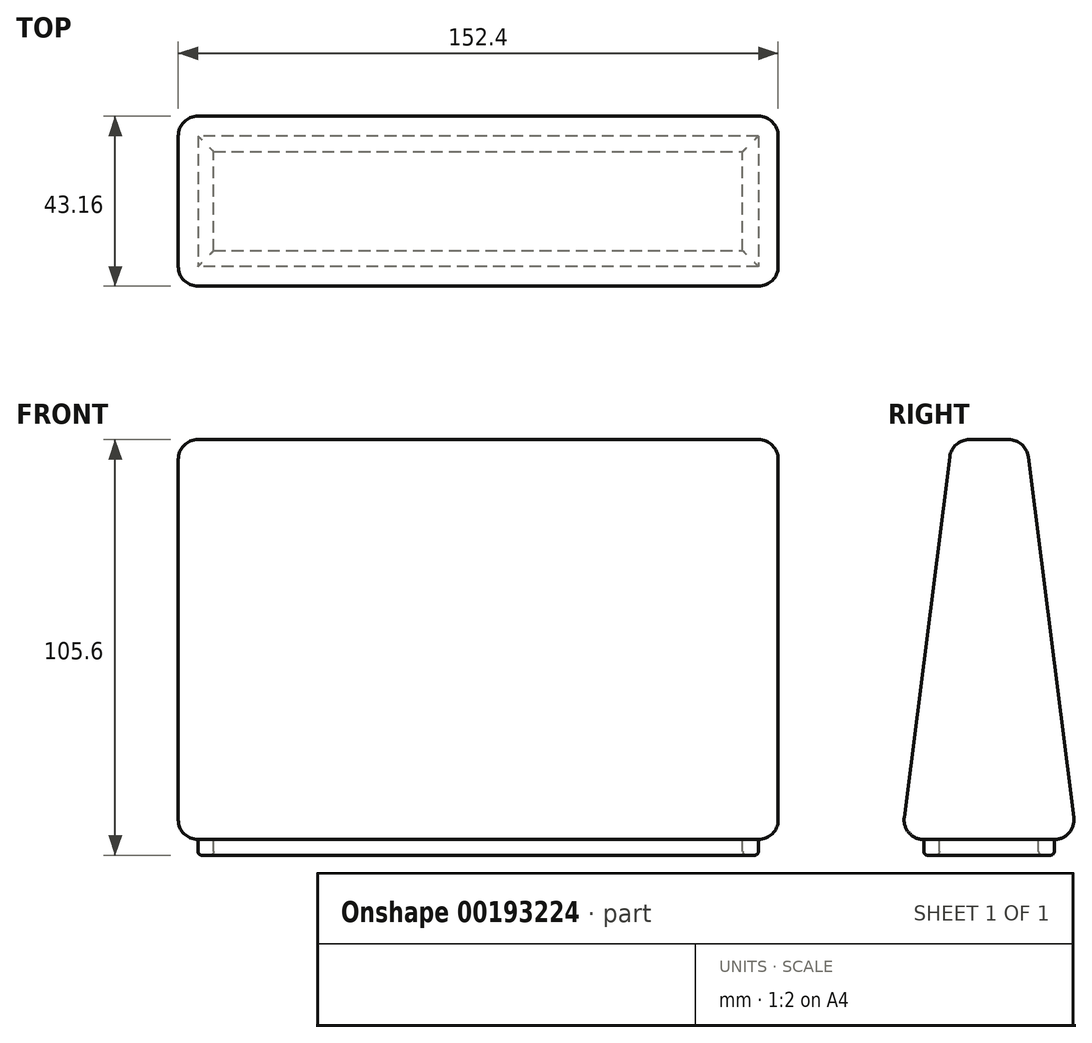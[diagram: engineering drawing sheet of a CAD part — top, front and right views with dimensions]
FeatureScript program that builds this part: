
annotation { "Feature Type Name" : "Feature", "Feature Type Description" : "" }
export const myFeature = defineFeature(function(context is Context, id is Id, definition is map)
    precondition{}
    {
        {
            var Q0;
            Q0=qCreatedBy(makeId("Right.planeOp"),FACE);
            var sketch = newSketch(context, id + "F0", { "sketchPlane" : qUnion([Q0])});
            skLineSegment(sketch, "E0", {"start": v(0, -83.95) * mm, "end": v(0, 33) * mm, "construction": true});
            skLineSegment(sketch, "E1", {"start": v(0, -83.95) * mm, "end": v(22.26, -83.95) * mm});
            skLineSegment(sketch, "E2", {"start": v(22.26, -83.95) * mm, "end": v(9.4, 17.65) * mm});
            skLineSegment(sketch, "E3", {"start": v(9.4, 17.65) * mm, "end": v(0, 17.65) * mm});
            skLineSegment(sketch, "E4.MirrorCS", {"start": v(0, -83.95) * mm, "end": v(-22.26, -83.95) * mm});
            skLineSegment(sketch, "E5.MirrorCS", {"start": v(-22.26, -83.95) * mm, "end": v(-9.4, 17.65) * mm});
            skLineSegment(sketch, "E6.MirrorCS", {"start": v(-9.4, 17.65) * mm, "end": v(0, 17.65) * mm});
            skSolve(sketch);
        }
        {
            var Q0;
            Q0=makeQuery(id+"F0.imprint","IMPRINT",FACE,{"disambiguationData":[TD([[makeQuery(id+"F0.imprint","IMPRINT",EDGE,{"derivedFrom":sQuery(id+"F0.wireOp",EDGE,"E1")}),1.0]])]});
            extrude(context, id + "F1", {"entities" : qUnion([Q0]), "depth" : 152.4 * mm});
        }
        {
            var Q0;
            Q0=makeQuery(id+"F1.opExtrude","SWEPT_FACE",FACE,{"disambiguationData":[OSD([sQuery(id+"F0.wireOp",EDGE,"E2")])]});
            var Q1;
            Q1=makeQuery(id+"F1.opExtrude","SWEPT_FACE",FACE,{"disambiguationData":[OSD([sQuery(id+"F0.wireOp",EDGE,"E5.MirrorCS")])]});
            var Q2;
            Q2=makeQuery(id+"F1.opExtrude","SWEPT_FACE",FACE,{"disambiguationData":[OSD([sQuery(id+"F0.wireOp",EDGE,"E3"),sQuery(id+"F0.wireOp",EDGE,"E6.MirrorCS")])]});
            var Q3;
            Q3=makeQuery(id+"F1.opExtrude","SWEPT_EDGE",EDGE,{"disambiguationData":[OSD([sQuery(id+"F0.wireOp",EDGE,"E5.MirrorCS"),sQuery(id+"F0.wireOp",EDGE,"E6.MirrorCS")])]});
            var Q4;
            Q4=makeQuery(id+"F1.opExtrude","SWEPT_EDGE",EDGE,{"disambiguationData":[OSD([sQuery(id+"F0.wireOp",EDGE,"E4.MirrorCS"),sQuery(id+"F0.wireOp",EDGE,"E5.MirrorCS")])]});
            var Q5;
            Q5=makeQuery(id+"F1.opExtrude","CAP_FACE",FACE,{"disambiguationData":[OSD([sQuery(id+"F0.wireOp",EDGE,"E1"),sQuery(id+"F0.wireOp",EDGE,"E2"),sQuery(id+"F0.wireOp",EDGE,"E3"),sQuery(id+"F0.wireOp",EDGE,"E4.MirrorCS"),sQuery(id+"F0.wireOp",EDGE,"E5.MirrorCS"),sQuery(id+"F0.wireOp",EDGE,"E6.MirrorCS")])],"isStart":false});
            var Q6;
            Q6=makeQuery(id+"F1.opExtrude","SWEPT_EDGE",EDGE,{"disambiguationData":[OSD([sQuery(id+"F0.wireOp",EDGE,"E2"),sQuery(id+"F0.wireOp",EDGE,"E3")])]});
            var Q7;
            Q7=makeQuery(id+"F1.opExtrude","CAP_FACE",FACE,{"disambiguationData":[OSD([sQuery(id+"F0.wireOp",EDGE,"E1"),sQuery(id+"F0.wireOp",EDGE,"E2"),sQuery(id+"F0.wireOp",EDGE,"E3"),sQuery(id+"F0.wireOp",EDGE,"E4.MirrorCS"),sQuery(id+"F0.wireOp",EDGE,"E5.MirrorCS"),sQuery(id+"F0.wireOp",EDGE,"E6.MirrorCS")])],"isStart":true});
            var Q8;
            Q8=makeQuery(id+"F1.opExtrude","CAP_EDGE",EDGE,{"disambiguationData":[OSD([sQuery(id+"F0.wireOp",EDGE,"E5.MirrorCS")])],"isStart":true});
            var Q9;
            Q9=makeQuery(id+"F1.opExtrude","CAP_EDGE",EDGE,{"disambiguationData":[OSD([sQuery(id+"F0.wireOp",EDGE,"E5.MirrorCS")])],"isStart":false});
            var Q10;
            Q10=makeQuery(id+"F1.opExtrude","CAP_EDGE",EDGE,{"disambiguationData":[OSD([sQuery(id+"F0.wireOp",EDGE,"E2")])],"isStart":true});
            var Q11;
            Q11=makeQuery(id+"F1.opExtrude","CAP_EDGE",EDGE,{"disambiguationData":[OSD([sQuery(id+"F0.wireOp",EDGE,"E1"),sQuery(id+"F0.wireOp",EDGE,"E4.MirrorCS")])],"isStart":true});
            var Q12;
            Q12=makeQuery(id+"F1.opExtrude","CAP_EDGE",EDGE,{"disambiguationData":[OSD([sQuery(id+"F0.wireOp",EDGE,"E1"),sQuery(id+"F0.wireOp",EDGE,"E4.MirrorCS")])],"isStart":false});
            var Q13;
            Q13=makeQuery(id+"F1.opExtrude","SWEPT_FACE",FACE,{"disambiguationData":[OSD([sQuery(id+"F0.wireOp",EDGE,"E1"),sQuery(id+"F0.wireOp",EDGE,"E4.MirrorCS")])]});
            var Q14;
            Q14=makeQuery(id+"F1.opExtrude","SWEPT_EDGE",EDGE,{"disambiguationData":[OSD([sQuery(id+"F0.wireOp",EDGE,"E1"),sQuery(id+"F0.wireOp",EDGE,"E2")])]});
            var Q15;
            Q15=makeQuery(id+"F1.opExtrude","CAP_EDGE",EDGE,{"disambiguationData":[OSD([sQuery(id+"F0.wireOp",EDGE,"E2")])],"isStart":false});
            var Q16;
            Q16=makeQuery(id+"F1.opExtrude","CAP_EDGE",EDGE,{"disambiguationData":[OSD([sQuery(id+"F0.wireOp",EDGE,"E3"),sQuery(id+"F0.wireOp",EDGE,"E6.MirrorCS")])],"isStart":true});
            var Q17;
            Q17=makeQuery(id+"F1.opExtrude","CAP_EDGE",EDGE,{"disambiguationData":[OSD([sQuery(id+"F0.wireOp",EDGE,"E3"),sQuery(id+"F0.wireOp",EDGE,"E6.MirrorCS")])],"isStart":false});
            fillet(context, id + "F2", {"entities" : qUnion([Q0, Q1, Q2, Q3, Q4, Q5, Q6, Q7, Q8, Q9, Q10, Q11, Q12, Q13, Q14, Q15, Q16, Q17]), "radius" : 5 * mm, "tangentPropagation" : true, "allowEdgeOverflow" : false});
        }
        {
            var Q0;
            Q0=makeQuery(id+"F1.opExtrude","SWEPT_FACE",FACE,{"disambiguationData":[OSD([sQuery(id+"F0.wireOp",EDGE,"E1"),sQuery(id+"F0.wireOp",EDGE,"E4.MirrorCS")])]});
            var sketch = newSketch(context, id + "F3", { "sketchPlane" : qUnion([Q0])});
            skLineSegment(sketch, "E7.bottom", {"start": v(5, 16.58) * mm, "end": v(147.4, 16.58) * mm});
            skLineSegment(sketch, "E7.top", {"start": v(5, -16.58) * mm, "end": v(147.4, -16.58) * mm});
            skLineSegment(sketch, "E7.left", {"start": v(5, 16.58) * mm, "end": v(5, -16.58) * mm});
            skLineSegment(sketch, "E7.right", {"start": v(147.4, 16.58) * mm, "end": v(147.4, -16.58) * mm});
            skLineSegment(sketch, "E8.0", {"start": v(9, 12.58) * mm, "end": v(9, -12.58) * mm});
            skLineSegment(sketch, "E8.1", {"start": v(9, 12.58) * mm, "end": v(143.4, 12.58) * mm});
            skLineSegment(sketch, "E8.2", {"start": v(143.4, 12.58) * mm, "end": v(143.4, -12.58) * mm});
            skLineSegment(sketch, "E8.3", {"start": v(9, -12.58) * mm, "end": v(143.4, -12.58) * mm});
            skSolve(sketch);
        }
        {
            var Q0;
            Q0 = qSketchRegion(id + "F3", true);
            extrude(context, id + "F4", {"entities" : qUnion([Q0]), "operationType" : NewBodyOperationType.ADD, "depth" : 4 * mm});
        }
        {
            var Q0;
            Q0=makeQuery(id+"F4.opExtrude","CAP_FACE",FACE,{"disambiguationData":[OSD([sQuery(id+"F3.wireOp",EDGE,"E7.bottom"),sQuery(id+"F3.wireOp",EDGE,"E7.top"),sQuery(id+"F3.wireOp",EDGE,"E7.left"),sQuery(id+"F3.wireOp",EDGE,"E7.right"),sQuery(id+"F3.wireOp",EDGE,"E8.0"),sQuery(id+"F3.wireOp",EDGE,"E8.1"),sQuery(id+"F3.wireOp",EDGE,"E8.2"),sQuery(id+"F3.wireOp",EDGE,"E8.3")])],"isStart":false});
            fillet(context, id + "F5", {"entities" : qUnion([Q0]), "radius" : 1 * mm, "tangentPropagation" : true, "allowEdgeOverflow" : false});
        }
    });
